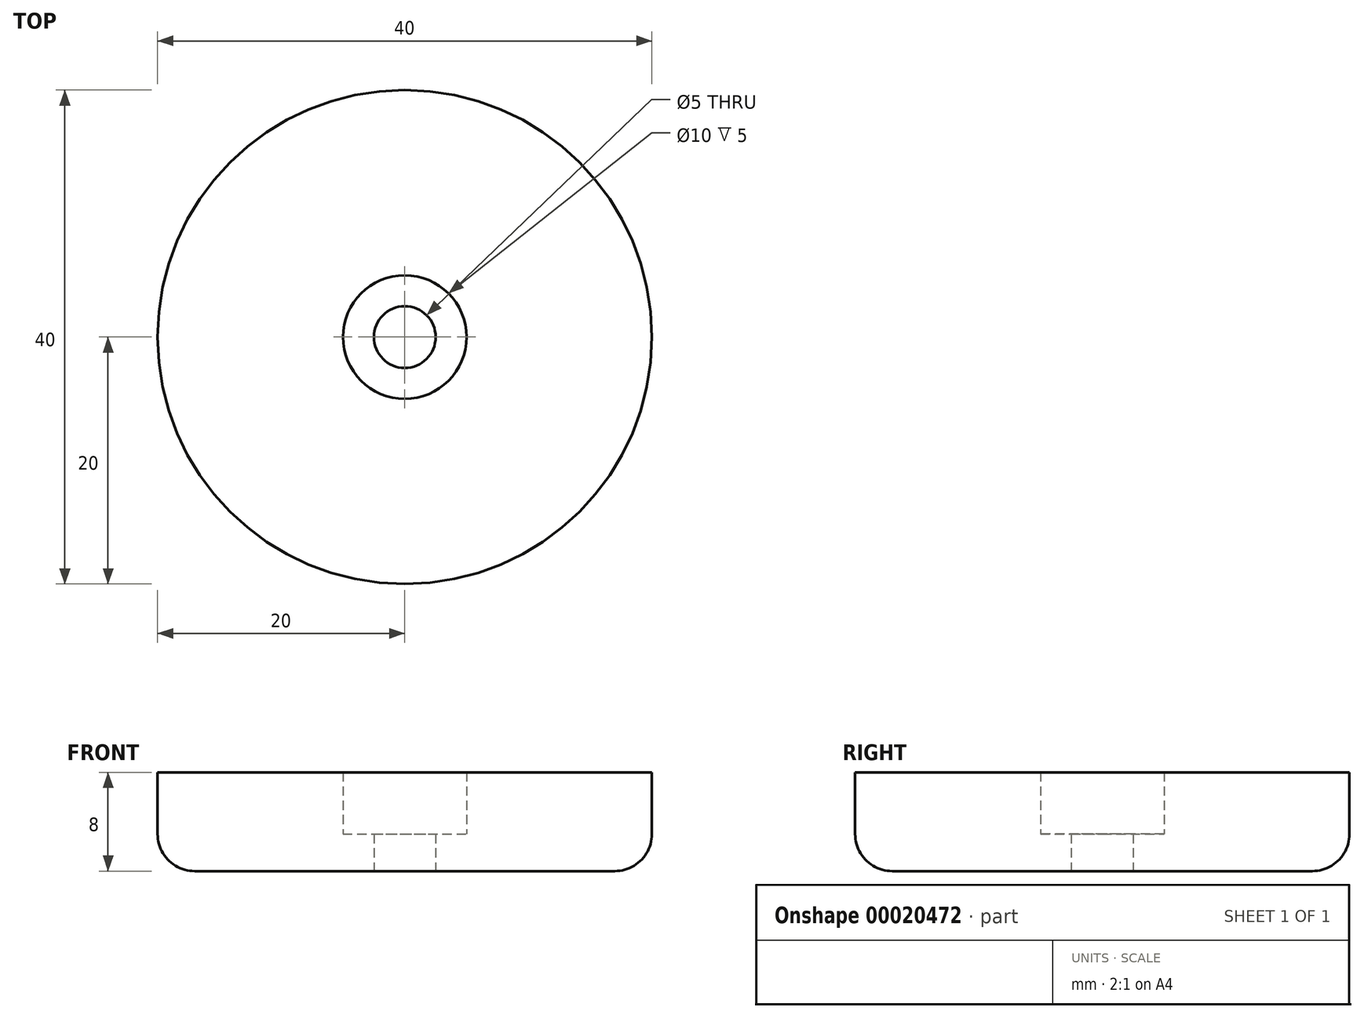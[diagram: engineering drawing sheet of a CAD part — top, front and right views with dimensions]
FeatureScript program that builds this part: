
annotation { "Feature Type Name" : "Feature", "Feature Type Description" : "" }
export const myFeature = defineFeature(function(context is Context, id is Id, definition is map)
    precondition{}
    {
        {
            var Q0;
            Q0=qCreatedBy(makeId("Top.planeOp"),FACE);
            var sketch = newSketch(context, id + "F0", { "sketchPlane" : qUnion([Q0])});
            skCircle(sketch, "E0", {"center": v(0, 0) * mm, "radius": 20 * mm});
            skSolve(sketch);
        }
        {
            var Q0;
            Q0 = qSketchRegion(id + "F0", true);
            extrude(context, id + "F1", {"entities" : qUnion([Q0]), "depth" : 8 * mm});
        }
        {
            var Q0;
            Q0=makeQuery(id+"F1.opExtrude","CAP_FACE",FACE,{"disambiguationData":[OSD([sQuery(id+"F0.wireOp",EDGE,"E0")])],"isStart":false});
            var sketch = newSketch(context, id + "F2", { "sketchPlane" : qUnion([Q0])});
            skCircle(sketch, "E1", {"center": v(0, 0) * mm, "radius": 19 * mm});
            skSolve(sketch);
        }
        {
            var Q0;
            Q0=makeQuery(id+"F1.opExtrude","CAP_EDGE",EDGE,{"disambiguationData":[OSD([sQuery(id+"F0.wireOp",EDGE,"E0")])],"isStart":true});
            fillet(context, id + "F3", {"entities" : qUnion([Q0]), "radius" : 3 * mm, "tangentPropagation" : true, "allowEdgeOverflow" : false});
        }
        {
            var Q0;
            Q0=makeQuery(id+"F2.imprint","IMPRINT",FACE,{"disambiguationData":[TD([[makeQuery(id+"F2.imprint","IMPRINT",EDGE,{"derivedFrom":sQuery(id+"F2.wireOp",EDGE,"E1")}),1.0]])]});
            var sketch = newSketch(context, id + "F4", { "sketchPlane" : qUnion([Q0])});
            skCircle(sketch, "E2", {"center": v(0, 0) * mm, "radius": 4 * mm});
            skSolve(sketch);
        }
        {
            var Q0;
            Q0=sQuery(id+"F4.wireOp",VERTEX,"E2.center");
            var Q1;
            Q1=makeQuery(id+"F1.opExtrude","SWEPT_BODY",BODY,{"disambiguationData":[OSD([sQuery(id+"F0.wireOp",EDGE,"E0")])]});
            hole(context, id + "F5", {"style" : HoleStyle.C_BORE, "holeDiameter" : 5 * mm, "cBoreDiameter" : 10 * mm, "cBoreDepth" : 5 * mm, "endStyle" : HoleEndStyle.THROUGH, "locations" : qUnion([Q0]), "scope" : qUnion([Q1])});
        }
    });
